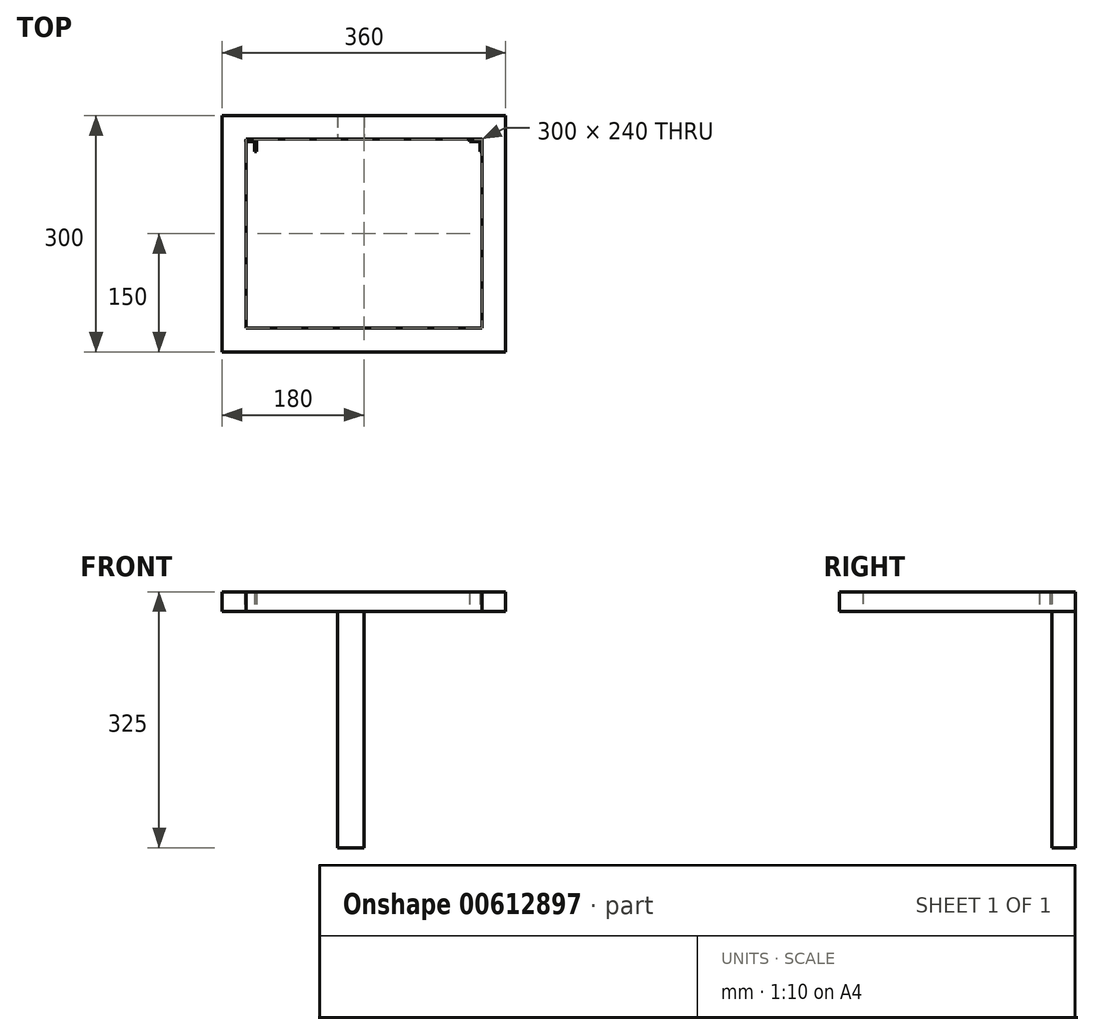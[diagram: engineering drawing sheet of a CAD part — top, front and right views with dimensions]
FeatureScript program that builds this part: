
annotation { "Feature Type Name" : "Feature", "Feature Type Description" : "" }
export const myFeature = defineFeature(function(context is Context, id is Id, definition is map)
    precondition{}
    {
        {
            var Q0;
            Q0=qCreatedBy(makeId("Top.planeOp"),FACE);
            var sketch = newSketch(context, id + "F0", { "sketchPlane" : qUnion([Q0])});
            skLineSegment(sketch, "E0.bottom", {"start": v(-150, -150) * mm, "end": v(150, -150) * mm});
            skLineSegment(sketch, "E0.top", {"start": v(-150, 150) * mm, "end": v(150, 150) * mm});
            skLineSegment(sketch, "E0.left", {"start": v(-150, -150) * mm, "end": v(-150, 150) * mm});
            skLineSegment(sketch, "E0.right", {"start": v(150, -150) * mm, "end": v(150, 150) * mm});
            skLineSegment(sketch, "E1.top", {"start": v(-150, -120) * mm, "end": v(150, -120) * mm});
            skLineSegment(sketch, "E1.left", {"start": v(-150, -150) * mm, "end": v(-150, -120) * mm});
            skLineSegment(sketch, "E1.right", {"start": v(150, -150) * mm, "end": v(150, -120) * mm});
            skLineSegment(sketch, "E2", {"start": v(0, 0) * mm, "end": v(-150, 0) * mm});
            skLineSegment(sketch, "E3.MirrorCS", {"start": v(-150, 120) * mm, "end": v(150, 120) * mm});
            skLineSegment(sketch, "E4.bottom", {"start": v(-150, 150) * mm, "end": v(-180, 150) * mm});
            skLineSegment(sketch, "E4.top", {"start": v(-150, -149.96) * mm, "end": v(-180, -149.96) * mm});
            skLineSegment(sketch, "E4.left", {"start": v(-150, 150) * mm, "end": v(-150, -149.96) * mm});
            skLineSegment(sketch, "E4.right", {"start": v(-180, 150) * mm, "end": v(-180, -149.96) * mm});
            skLineSegment(sketch, "E5", {"start": v(0, 0) * mm, "end": v(0, -150) * mm});
            skLineSegment(sketch, "E6.MirrorCS", {"start": v(180, 150) * mm, "end": v(180, -149.96) * mm});
            skLineSegment(sketch, "E7.MirrorCS", {"start": v(150, 150) * mm, "end": v(180, 150) * mm});
            skLineSegment(sketch, "E8.MirrorCS", {"start": v(150, -149.96) * mm, "end": v(180, -149.96) * mm});
            skLineSegment(sketch, "E9.MirrorCS", {"start": v(150, 150) * mm, "end": v(150, -149.96) * mm});
            skSolve(sketch);
        }
        {
            var Q0;
            {var subQ0=sQuery(id+"F0.wireOp",EDGE,"E0.top");Q0=makeQuery(id+"F0.imprint","IMPRINT",FACE,{"disambiguationData":[TD([[makeQuery(id+"F0.imprint","IMPRINT",EDGE,{"derivedFrom":subQ0}),-1.0]])]});}
            var Q1;
            Q1=makeQuery(id+"F0.imprint","IMPRINT",FACE,{"disambiguationData":[TD([[makeQuery(id+"F0.imprint","IMPRINT",EDGE,{"derivedFrom":sQuery(id+"F0.wireOp",EDGE,"E0.bottom")}),1.0]])]});
            var Q2;
            Q2=makeQuery(id+"F0.imprint","IMPRINT",FACE,{"disambiguationData":[TD([[makeQuery(id+"F0.imprint","IMPRINT",EDGE,{"derivedFrom":sQuery(id+"F0.wireOp",EDGE,"E6.MirrorCS")}),-1.0]])]});
            var Q3;
            {var subQ3=sQuery(id+"F0.wireOp",EDGE,"E4.bottom");Q3=makeQuery(id+"F0.imprint","IMPRINT",FACE,{"disambiguationData":[TD([[makeQuery(id+"F0.imprint","IMPRINT",EDGE,{"derivedFrom":subQ3}),1.0]])]});}
            extrude(context, id + "F1", {"entities" : qUnion([Q0, Q1, Q2, Q3]), "depth" : 25 * mm, "offsetDistance" : 25 * mm});
        }
        {
            var Q0;
            Q0=makeQuery(id+"F1.opExtrude","CAP_FACE",FACE,{"disambiguationData":[OSD([sQuery(id+"F0.wireOp",EDGE,"E0.top"),sQuery(id+"F0.wireOp",EDGE,"E0.bottom"),sQuery(id+"F0.wireOp",EDGE,"E1.top"),sQuery(id+"F0.wireOp",EDGE,"E3.MirrorCS"),sQuery(id+"F0.wireOp",EDGE,"E4.bottom"),sQuery(id+"F0.wireOp",EDGE,"E4.top"),sQuery(id+"F0.wireOp",EDGE,"E4.left"),sQuery(id+"F0.wireOp",EDGE,"E4.right"),sQuery(id+"F0.wireOp",EDGE,"E6.MirrorCS"),sQuery(id+"F0.wireOp",EDGE,"E7.MirrorCS"),sQuery(id+"F0.wireOp",EDGE,"E8.MirrorCS"),sQuery(id+"F0.wireOp",EDGE,"E9.MirrorCS")])],"isStart":true});
            var sketch = newSketch(context, id + "F2", { "sketchPlane" : qUnion([Q0])});
            skLineSegment(sketch, "E10", {"start": v(150, 120) * mm, "end": v(150, 149.96) * mm});
            skLineSegment(sketch, "E11", {"start": v(150, -120) * mm, "end": v(150, -150) * mm});
            skLineSegment(sketch, "E12", {"start": v(-150, -120) * mm, "end": v(-150, -150) * mm});
            skLineSegment(sketch, "E13", {"start": v(-150, 120) * mm, "end": v(-150, 149.96) * mm});
            skSolve(sketch);
        }
        {
            var Q0;
            Q0=makeQuery(id+"F2.imprint","IMPRINT",FACE,{"disambiguationData":[TD([[makeQuery(id+"F2.imprint","IMPRINT",EDGE,{"derivedFrom":makeQuery(id+"F1.opExtrude","CAP_EDGE",EDGE,{"disambiguationData":[OSD([sQuery(id+"F0.wireOp",EDGE,"E1.top")])],"isStart":true})}),-1.0]])]});
            var sketch = newSketch(context, id + "F3", { "sketchPlane" : qUnion([Q0])});
            skLineSegment(sketch, "E14.bottom", {"start": v(149.36, -119.31) * mm, "end": v(147.36, -119.31) * mm});
            skLineSegment(sketch, "E14.top", {"start": v(149.36, -104.31) * mm, "end": v(147.36, -104.31) * mm});
            skLineSegment(sketch, "E14.left", {"start": v(147.36, -119.31) * mm, "end": v(147.36, -104.31) * mm});
            skLineSegment(sketch, "E14.right", {"start": v(149.36, -119.31) * mm, "end": v(149.36, -104.31) * mm});
            skLineSegment(sketch, "E15.bottom", {"start": v(149.36, -119.31) * mm, "end": v(134.36, -119.31) * mm});
            skLineSegment(sketch, "E15.top", {"start": v(149.36, -117.31) * mm, "end": v(134.36, -117.31) * mm});
            skLineSegment(sketch, "E15.left", {"start": v(149.36, -119.31) * mm, "end": v(149.36, -117.31) * mm});
            skLineSegment(sketch, "E15.right", {"start": v(134.36, -119.31) * mm, "end": v(134.36, -117.31) * mm});
            skSolve(sketch);
        }
        {
            var Q0;
            Q0 = qSketchRegion(id + "F3", true);
            extrude(context, id + "F4", {"entities" : qUnion([Q0]), "oppositeDirection" : true, "depth" : 24.3 * mm, "offsetDistance" : 25 * mm});
        }
        {
            var Q0;
            Q0=makeQuery(id+"F4.opExtrude","SWEPT_BODY",BODY,{"disambiguationData":[OSD([sQuery(id+"F3.wireOp",EDGE,"E14.top"),sQuery(id+"F3.wireOp",EDGE,"E14.left"),sQuery(id+"F3.wireOp",EDGE,"E14.right"),sQuery(id+"F3.wireOp",EDGE,"E15.bottom"),sQuery(id+"F3.wireOp",EDGE,"E15.top"),sQuery(id+"F3.wireOp",EDGE,"E15.left"),sQuery(id+"F3.wireOp",EDGE,"E15.right")])]});
            transform(context, id + "F5", {"entities" : qUnion([Q0]), "transformType" : TransformType.TRANSLATION_3D, "dx" : -286 * mm, "dy" : 0 * mm, "dz" : 0 * mm, "makeCopy" : true});
        }
        {
            var Q0;
            {var subQ0=sQuery(id+"F2.wireOp",EDGE,"E11");Q0=makeQuery(id+"F2.imprint","IMPRINT",FACE,{"disambiguationData":[TD([[makeQuery(id+"F2.imprint","IMPRINT",EDGE,{"derivedFrom":subQ0}),-1.0]])]});}
            var sketch = newSketch(context, id + "F6", { "sketchPlane" : qUnion([Q0])});
            skLineSegment(sketch, "E16.bottom", {"start": v(-33.22, -149.93) * mm, "end": v(0, -149.93) * mm});
            skLineSegment(sketch, "E16.top", {"start": v(-33.22, -120.16) * mm, "end": v(0, -120.16) * mm});
            skLineSegment(sketch, "E16.left", {"start": v(-33.22, -149.93) * mm, "end": v(-33.22, -120.16) * mm});
            skLineSegment(sketch, "E16.right", {"start": v(0, -149.93) * mm, "end": v(0, -120.16) * mm});
            skSolve(sketch);
        }
        {
            var Q0;
            Q0 = qSketchRegion(id + "F6", true);
            extrude(context, id + "F7", {"entities" : qUnion([Q0]), "operationType" : NewBodyOperationType.ADD, "depth" : 300 * mm, "offsetDistance" : 25 * mm});
        }
    });
